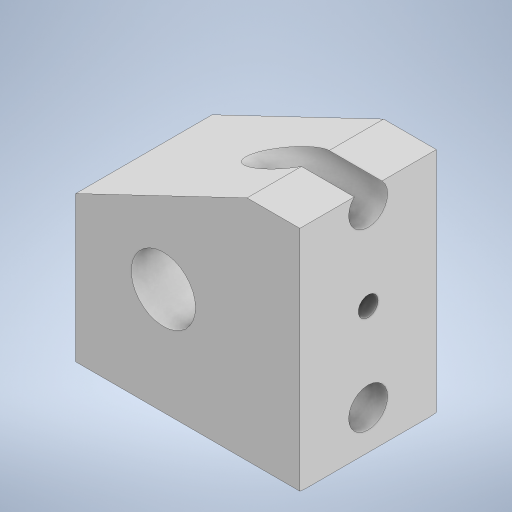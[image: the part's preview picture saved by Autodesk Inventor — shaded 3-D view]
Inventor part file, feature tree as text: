
AUTODESK INVENTOR PART (.ipt)
format: ipt  version: 2024 (Build 280153000, 153)  size: 240,128 bytes
history: native  units: in
note: dims shown in document units (in); Inventor stores cm internally (conversion verified against a paired STEP export)
features: other x3, extrude x1, sketch x1
ambient origin geometry x8: Origin, YZ Plane, XZ Plane, XY Plane, X Axis, Y Axis, Z Axis, Center Point
bodies: Body1 (feature_tree)
feature tree (5):
  other  "lower.ipt"
  extrude  "Extrusion1"  Depth=0.04in
  other  "Solid12::lower.ipt"
  other  "TaggingFeature1"
  sketch  "Sketch1"  dims[d0=0.3937in d1=0.04in d2=0.04in d3=0.0in]
